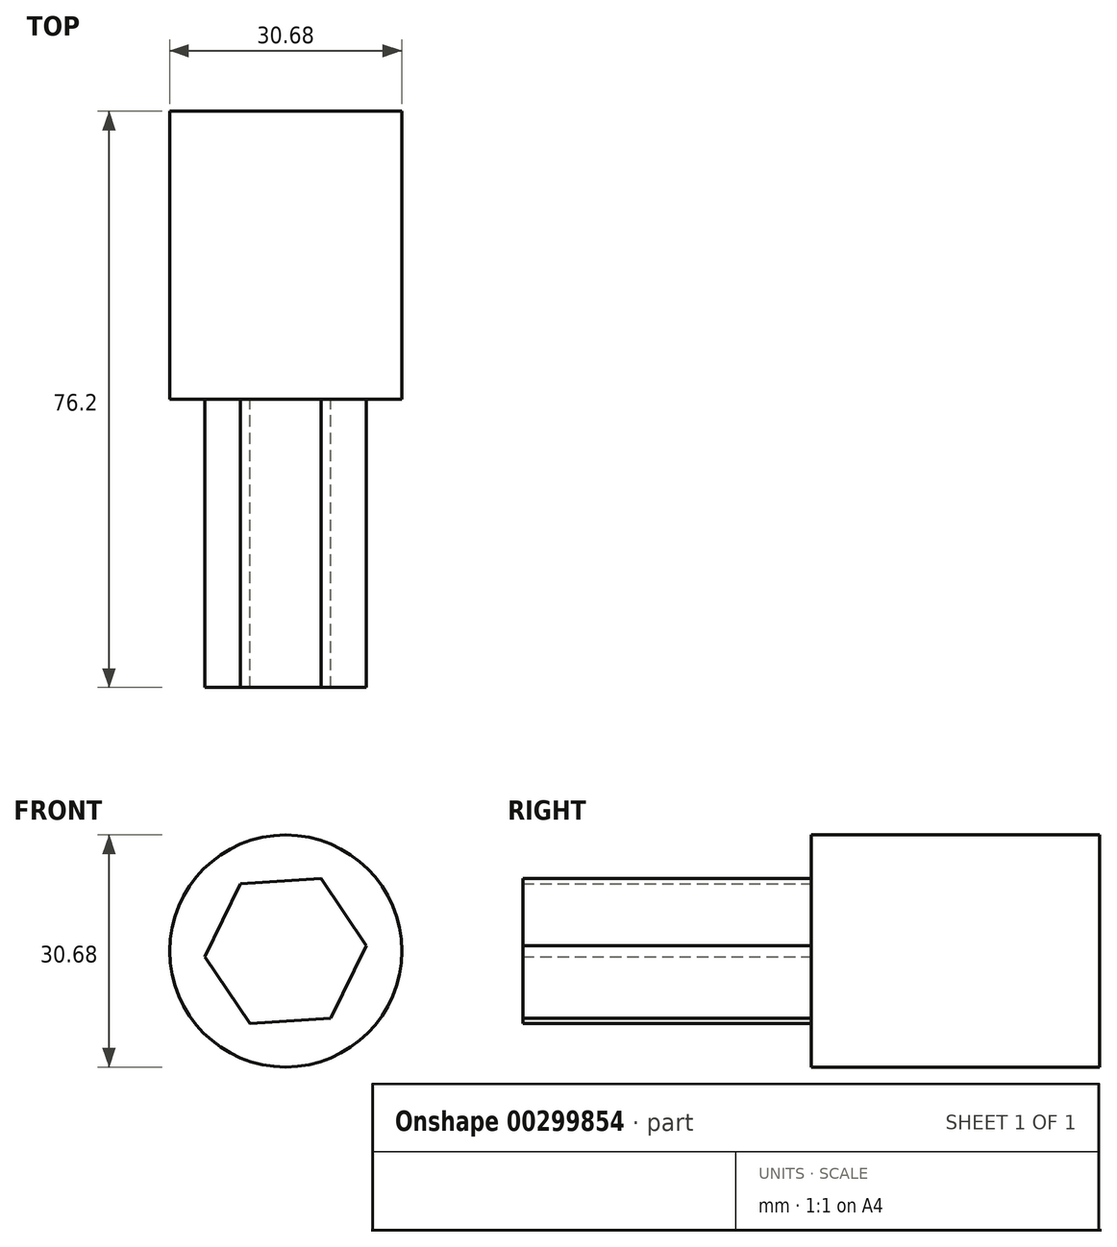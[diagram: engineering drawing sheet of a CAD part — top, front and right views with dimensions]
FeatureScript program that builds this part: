
annotation { "Feature Type Name" : "Feature", "Feature Type Description" : "" }
export const myFeature = defineFeature(function(context is Context, id is Id, definition is map)
    precondition{}
    {
        {
            var Q0;
            Q0=qCreatedBy(makeId("Front.planeOp"),FACE);
            var sketch = newSketch(context, id + "F0", { "sketchPlane" : qUnion([Q0])});
            skCircle(sketch, "E0.cCircle", {"center": v(0, 0) * mm, "radius": 9.27 * mm, "construction": true});
            skLineSegment(sketch, "E0.0", {"start": v(4.7, 9.62) * mm, "end": v(10.68, 0.73) * mm});
            skLineSegment(sketch, "E0.1", {"start": v(10.68, 0.73) * mm, "end": v(5.97, -8.89) * mm});
            skLineSegment(sketch, "E0.2", {"start": v(5.97, -8.89) * mm, "end": v(-4.7, -9.62) * mm});
            skLineSegment(sketch, "E0.3", {"start": v(-4.7, -9.62) * mm, "end": v(-10.68, -0.73) * mm});
            skLineSegment(sketch, "E0.4", {"start": v(-10.68, -0.73) * mm, "end": v(-5.97, 8.89) * mm});
            skLineSegment(sketch, "E0.5", {"start": v(-5.97, 8.89) * mm, "end": v(4.7, 9.62) * mm});
            skPoint(sketch, "E0.0.midPoint", {"position": v(7.7, 5.17) * mm});
            skSolve(sketch);
        }
        {
            var Q0;
            Q0=makeQuery(id+"F0.imprint","IMPRINT",FACE,{"disambiguationData":[TD([[makeQuery(id+"F0.imprint","IMPRINT",EDGE,{"derivedFrom":sQuery(id+"F0.wireOp",EDGE,"E0.0")}),-1.0]])]});
            extrude(context, id + "F1", {"entities" : qUnion([Q0]), "depth" : 38.1 * mm});
        }
        {
            var Q0;
            Q0=qCreatedBy(makeId("Front.planeOp"),FACE);
            var sketch = newSketch(context, id + "F2", { "sketchPlane" : qUnion([Q0])});
            skCircle(sketch, "E1", {"center": v(0, 0) * mm, "radius": 15.34 * mm});
            skSolve(sketch);
        }
        {
            var Q0;
            Q0 = qSketchRegion(id + "F2", true);
            extrude(context, id + "F3", {"entities" : qUnion([Q0]), "operationType" : NewBodyOperationType.ADD, "oppositeDirection" : true, "depth" : 38.1 * mm});
        }
    });
